FCSTD DOCUMENT  (FreeCAD 0.21R33694 (Git))
Label: land-marking-calculation
License: All rights reserved
LicenseURL: http://en.wikipedia.org/wiki/All_rights_reserved
objects: Sketcher::SketchObject×2, PartDesign::Body×1
note: 3 computed .brp shape members not serialized (recipe doc carries the construction recipe); baked Part::Feature solids carry a one-line shape summary decoded from their .brp

FEATURE [Sketcher::SketchObject] Sketch
  FullyConstrained = true
  MapMode = 5
  Support = -> [XY_Plane]
  sketch-geometry (13):
    g0: LineSegment StartX=3.6e-15 StartY=-6.7e-15 StartZ=0 EndX=865.999 EndY=-1.39277 EndZ=0
    g1: LineSegment StartX=865.999 StartY=-1.39277 StartZ=0 EndX=893.591 EndY=426.719 EndZ=0
    g2: LineSegment StartX=893.591 StartY=426.719 StartZ=0 EndX=30.6757 EndY=470 EndZ=0
    g3: LineSegment StartX=30.6757 StartY=470 StartZ=0 EndX=3.6e-15 EndY=0 EndZ=0
    g4: LineSegment StartX=30.6757 StartY=470 StartZ=0 EndX=30.6757 EndY=0 EndZ=0
    g5: LineSegment StartX=668.676 StartY=438 StartZ=0 EndX=668.676 EndY=0 EndZ=0
    g6: GeomPoint X=865.999 Y=1e-16 Z=0
    g7: GeomPoint X=30.6757 Y=-0.0493353 Z=0
    g8: GeomPoint X=30.6757 Y=438 Z=0
    g9: LineSegment StartX=30.6757 StartY=438 StartZ=0 EndX=668.676 EndY=438 EndZ=0
    g10: LineSegment StartX=893.591 StartY=426.719 StartZ=0 EndX=668.676 EndY=426.719 EndZ=0
    g11: LineSegment StartX=865.999 StartY=-1.39277 StartZ=0 EndX=865.999 EndY=426.719 EndZ=0
    g12: LineSegment StartX=893.591 StartY=426.719 StartZ=0 EndX=30.6757 EndY=426.719 EndZ=0
  constraints (50):
    c: Coincident(g-1,g0)
    c: Coincident(g0,g1)
    c: Coincident(g1,g2)
    c: Coincident(g2,g3)
    c: Coincident(g3,g0)
    c: Distance(g3) = 471
    c: Distance(g1) = 429
    c: Distance(g2) = 864
    c: Coincident(g4,g2)
    c: DistanceX(g4,g5) = 638
    c: PointOnObject(g5,g2)
    c: Distance(g0,g0) = 866
    c: DistanceY(g4,g4) = 470
    c: Parallel(g5,g4)
    c: PointOnObject(g4,g-1)
    c: PointOnObject(g5,g-1)
    c: Perpendicular(g4,g-1)
    c: Angle(g4,g-1) = 1.5708
    c: DistanceY(g5,g5) = 438
    c: PointOnObject(g6,g-1)
    c: Vertical(g0,g6)
    c: Distance(g6,g0) = 1.39277
    c: DistanceX(g5,g6) = 197.323
    c: DistanceX(g0,g4) = 30.6757
    c: PointOnObject(g7,g0)
    c: Vertical(g7,g4)
    c: DistanceY(g7,g4) = 0.0493353
    c: PointOnObject(g8,g4)
    c: Horizontal(g8,g5)
    c: DistanceY(g8,g2) = 32
    c: Coincident(g9,g8)
    c: Coincident(g9,g5)
    c: Coincident(g10,g1)
    c: PointOnObject(g10,g5)
    c: Perpendicular(g5,g10)
    c: Coincident(g11,g0)
    c: PointOnObject(g11,g10)
    c: Perpendicular(g10,g11)
    c: DistanceX(g10,g10) = 224.915
    c: DistanceY(g11,g11) = 428.112
    c: DistanceY(g10,g5) = 11.281
    c: DistanceX(g11,g1) = 27.5921
    c: Distance(g2,g5) = 638.802
    c: Angle(g0,g3) = 1.50723
    c: Angle(g1,g0) = 1.63355
    c: Coincident(g12,g1)
    c: PointOnObject(g12,g4)
    c: Horizontal(g12)
    c: DistanceX(g12,g12) = 862.915
    c: Angle(g2,g9) = 0.0501147
FEATURE [Sketcher::SketchObject] Sketch001
  FullyConstrained = true
  MapMode = 5
  Support = -> [XY_Plane]
  sketch-geometry (5):
    g0: LineSegment StartX=-9.5e-13 StartY=-5.162e-13 StartZ=0 EndX=132.665 EndY=25 EndZ=0
    g1: LineSegment StartX=132.665 StartY=25 StartZ=0 EndX=14.5027 EndY=109.04 EndZ=0
    g2: LineSegment StartX=14.5027 StartY=109.04 StartZ=0 EndX=-9.504e-13 EndY=-5.116e-13 EndZ=0
    g3: LineSegment StartX=14.5027 StartY=109.04 StartZ=0 EndX=33.8541 EndY=6.37963 EndZ=0
    g4: GeomPoint X=33.8541 Y=6.37963 Z=0
  constraints (16):
    c: Coincident(g-1,g0)
    c: Coincident(g0,g1)
    c: Coincident(g1,g2)
    c: Coincident(g2,g0)
    c: Coincident(g3,g1)
    c: PointOnObject(g3,g0)
    c: Distance(g2) = 110
    c: Distance(g1) = 145
    c: Distance(g0) = 135
    c: Distance(g0,g4) = 34.45
    c: Coincident(g3,g4)
    c: Angle(g0,g3) = 1.57085
    c: Angle(g0,g3) = 1.57085
    c: Angle(g0,g3) = 1.57085
    c: Angle(g0,g3) = 1.57085
    c: DistanceY(g-1,g0) = 25
FEATURE [PartDesign::Body] Body
  Group = -> [Sketch,Sketch001]
  Origin = -> Origin
